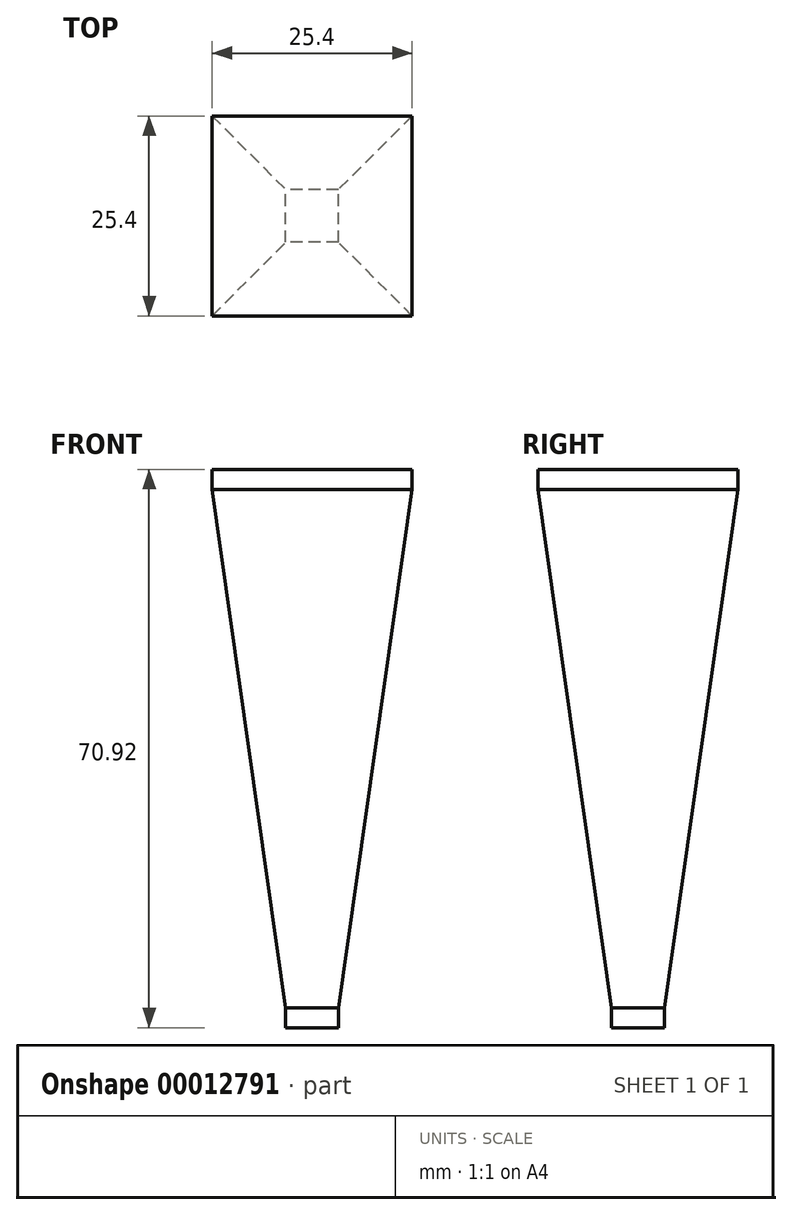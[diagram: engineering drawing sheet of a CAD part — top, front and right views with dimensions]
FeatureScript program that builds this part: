
annotation { "Feature Type Name" : "Feature", "Feature Type Description" : "" }
export const myFeature = defineFeature(function(context is Context, id is Id, definition is map)
    precondition{}
    {
        {
            var Q0;
            Q0=qCreatedBy(makeId("Top.planeOp"),FACE);
            var sketch = newSketch(context, id + "F0", { "sketchPlane" : qUnion([Q0])});
            skLineSegment(sketch, "E0.rect.bottom", {"start": v(12.7, -12.7) * mm, "end": v(-12.7, -12.7) * mm});
            skLineSegment(sketch, "E0.rect.top", {"start": v(12.7, 12.7) * mm, "end": v(-12.7, 12.7) * mm});
            skLineSegment(sketch, "E0.rect.left", {"start": v(12.7, -12.7) * mm, "end": v(12.7, 12.7) * mm});
            skLineSegment(sketch, "E0.rect.right", {"start": v(-12.7, -12.7) * mm, "end": v(-12.7, 12.7) * mm});
            skPoint(sketch, "E0.rect.middle", {"position": v(0, 0) * mm});
            skSolve(sketch);
        }
        {
            var Q0;
            Q0=qCreatedBy(makeId("Top.planeOp"),FACE);
            var sketch = newSketch(context, id + "F1", { "sketchPlane" : qUnion([Q0])});
            skLineSegment(sketch, "E1.rect.bottom", {"start": v(3.35, -3.35) * mm, "end": v(-3.35, -3.35) * mm});
            skLineSegment(sketch, "E1.rect.top", {"start": v(3.35, 3.35) * mm, "end": v(-3.35, 3.35) * mm});
            skLineSegment(sketch, "E1.rect.left", {"start": v(3.35, -3.35) * mm, "end": v(3.35, 3.35) * mm});
            skLineSegment(sketch, "E1.rect.right", {"start": v(-3.35, -3.35) * mm, "end": v(-3.35, 3.35) * mm});
            skPoint(sketch, "E1.rect.middle", {"position": v(0, 0) * mm});
            skSolve(sketch);
        }
        {
            var Q0;
            Q0 = qSketchRegion(id + "F0", true);
            extrude(context, id + "F2", {"entities" : qUnion([Q0]), "depth" : 2.54 * mm});
        }
        {
            var Q0;
            Q0 = qSketchRegion(id + "F1", true);
            extrude(context, id + "F3", {"entities" : qUnion([Q0]), "oppositeDirection" : true, "depth" : 2.54 * mm});
        }
        {
            var Q0;
            Q0=makeQuery(id+"F3.opExtrude","SWEPT_BODY",BODY,{"disambiguationData":[OSD([sQuery(id+"F1.wireOp",EDGE,"E1.rect.bottom"),sQuery(id+"F1.wireOp",EDGE,"E1.rect.top"),sQuery(id+"F1.wireOp",EDGE,"E1.rect.left"),sQuery(id+"F1.wireOp",EDGE,"E1.rect.right")])]});
            transform(context, id + "F4", {"entities" : qUnion([Q0]), "transformType" : TransformType.TRANSLATION_3D, "dx" : 0 * mm, "dy" : 0 * mm, "dz" : -65.84 * mm, "makeCopy" : false});
        }
        {
            var Q0;
            Q0=makeQuery(id+"F2.opExtrude","CAP_FACE",FACE,{"disambiguationData":[OSD([sQuery(id+"F0.wireOp",EDGE,"E0.rect.bottom"),sQuery(id+"F0.wireOp",EDGE,"E0.rect.top"),sQuery(id+"F0.wireOp",EDGE,"E0.rect.left"),sQuery(id+"F0.wireOp",EDGE,"E0.rect.right")])],"isStart":true});
            var Q1;
            Q1=makeQuery(id+"F3.opExtrude","CAP_FACE",FACE,{"disambiguationData":[OSD([sQuery(id+"F1.wireOp",EDGE,"E1.rect.bottom"),sQuery(id+"F1.wireOp",EDGE,"E1.rect.top"),sQuery(id+"F1.wireOp",EDGE,"E1.rect.left"),sQuery(id+"F1.wireOp",EDGE,"E1.rect.right")])],"isStart":true});
            loft(context, id + "F5", {"sheetProfilesArray" : [{ "sheetProfileEntities" : qUnion([Q0]) }, { "sheetProfileEntities" : qUnion([Q1]) }]});
        }
    });
